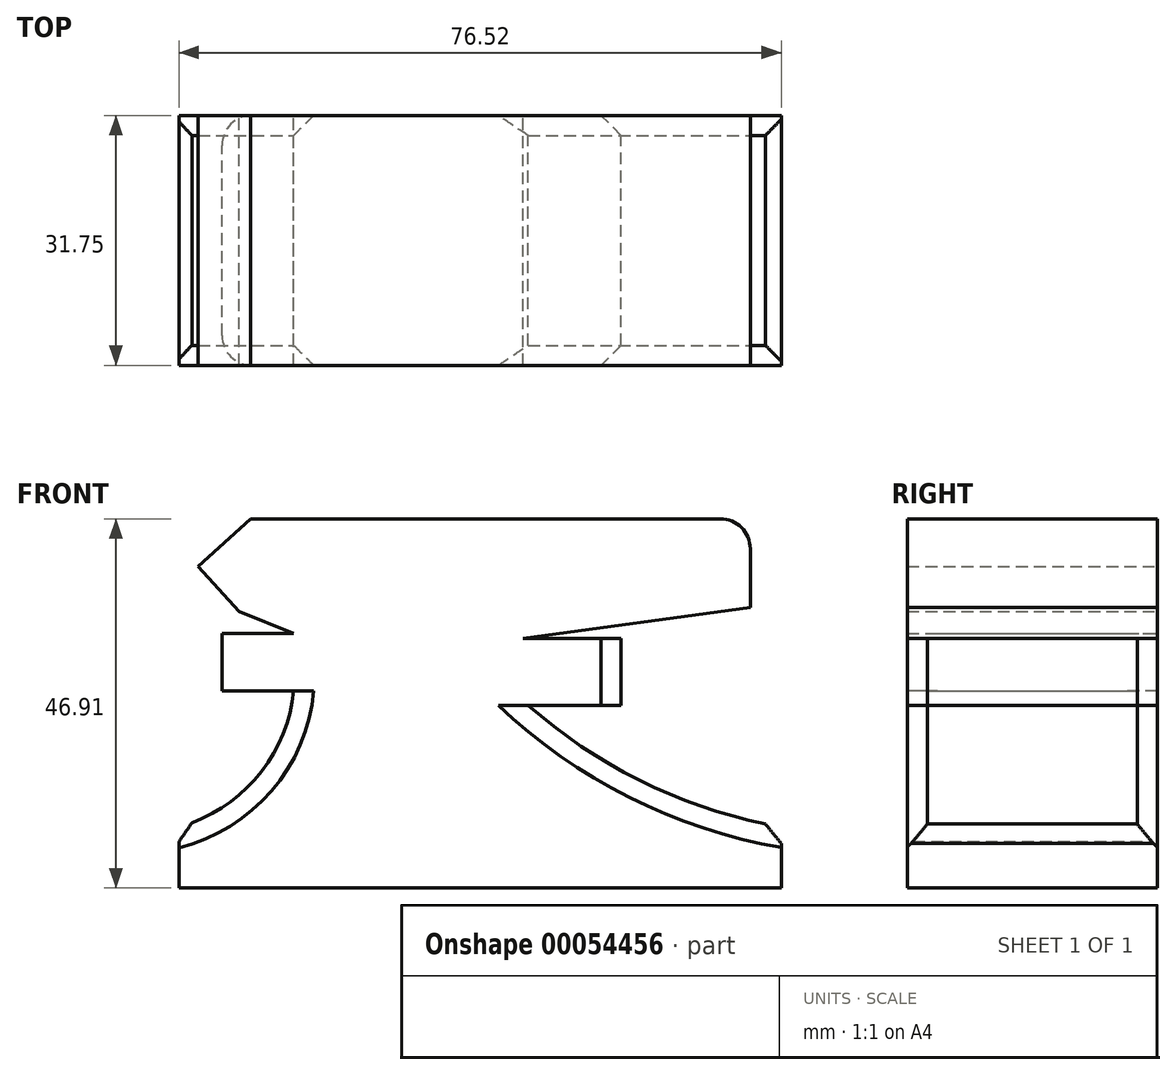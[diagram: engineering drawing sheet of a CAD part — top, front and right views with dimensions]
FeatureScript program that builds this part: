
annotation { "Feature Type Name" : "Feature", "Feature Type Description" : "" }
export const myFeature = defineFeature(function(context is Context, id is Id, definition is map)
    precondition{}
    {
        {
            var Q0;
            Q0=qCreatedBy(makeId("Front.planeOp"),FACE);
            var sketch = newSketch(context, id + "F0", { "sketchPlane" : qUnion([Q0])});
            skLineSegment(sketch, "E0", {"start": v(0, 0) * mm, "end": v(41.6, 0) * mm});
            skLineSegment(sketch, "E1", {"start": v(41.6, 0) * mm, "end": v(41.6, 7.74) * mm});
            skArc(sketch, "E2", {"start": v(9.41, 23.23) * mm, "mid": v(24.45, 13.28) * mm, "end": v(41.6, 7.74) * mm});
            skLineSegment(sketch, "E3", {"start": v(9.41, 23.23) * mm, "end": v(21.26, 23.23) * mm});
            skLineSegment(sketch, "E4", {"start": v(21.26, 23.23) * mm, "end": v(21.26, 31.73) * mm});
            skLineSegment(sketch, "E5", {"start": v(21.26, 31.73) * mm, "end": v(8.8, 31.73) * mm});
            skLineSegment(sketch, "E6", {"start": v(8.8, 31.73) * mm, "end": v(37.65, 35.68) * mm});
            skLineSegment(sketch, "E7", {"start": v(37.65, 35.68) * mm, "end": v(37.65, 46.91) * mm});
            skLineSegment(sketch, "E8", {"start": v(37.65, 46.91) * mm, "end": v(-25.8, 46.91) * mm});
            skLineSegment(sketch, "E9", {"start": v(-25.8, 46.91) * mm, "end": v(-32.49, 40.84) * mm});
            skLineSegment(sketch, "E10", {"start": v(-32.49, 40.84) * mm, "end": v(-27.31, 35.14) * mm});
            skLineSegment(sketch, "E11", {"start": v(-27.31, 35.14) * mm, "end": v(-20.34, 32.34) * mm});
            skLineSegment(sketch, "E12", {"start": v(-20.34, 32.34) * mm, "end": v(-29.45, 32.34) * mm});
            skLineSegment(sketch, "E13", {"start": v(-29.45, 32.34) * mm, "end": v(-29.45, 25.05) * mm});
            skLineSegment(sketch, "E14", {"start": v(-29.45, 25.05) * mm, "end": v(-20.34, 25.05) * mm});
            skArc(sketch, "E15", {"start": v(-34.92, 7.74) * mm, "mid": v(-24.96, 14.15) * mm, "end": v(-20.34, 25.05) * mm});
            skLineSegment(sketch, "E16", {"start": v(-34.92, 7.74) * mm, "end": v(-34.92, 0) * mm});
            skLineSegment(sketch, "E17", {"start": v(-34.92, 0) * mm, "end": v(0, 0) * mm});
            skSolve(sketch);
        }
        {
            var Q0;
            Q0=makeQuery(id+"F0.imprint","IMPRINT",FACE,{"disambiguationData":[TD([[makeQuery(id+"F0.imprint","IMPRINT",EDGE,{"derivedFrom":sQuery(id+"F0.wireOp",EDGE,"E0")}),1.0]])]});
            extrude(context, id + "F1", {"entities" : qUnion([Q0]), "depth" : 31.75 * mm});
        }
        {
            var Q0;
            Q0=makeQuery(id+"F1.opExtrude","CAP_EDGE",EDGE,{"disambiguationData":[OSD([sQuery(id+"F0.wireOp",EDGE,"E2")])],"isStart":false});
            var Q1;
            Q1=makeQuery(id+"F1.opExtrude","CAP_EDGE",EDGE,{"disambiguationData":[OSD([sQuery(id+"F0.wireOp",EDGE,"E2")])],"isStart":true});
            var Q2;
            Q2=makeQuery(id+"F1.opExtrude","CAP_EDGE",EDGE,{"disambiguationData":[OSD([sQuery(id+"F0.wireOp",EDGE,"E15")])],"isStart":false});
            var Q3;
            Q3=makeQuery(id+"F1.opExtrude","CAP_EDGE",EDGE,{"disambiguationData":[OSD([sQuery(id+"F0.wireOp",EDGE,"E15")])],"isStart":true});
            var Q4;
            Q4=makeQuery(id+"F1.opExtrude","SWEPT_EDGE",EDGE,{"disambiguationData":[OSD([sQuery(id+"F0.wireOp",EDGE,"E1"),sQuery(id+"F0.wireOp",EDGE,"E2")])]});
            var Q5;
            Q5=makeQuery(id+"F1.opExtrude","SWEPT_EDGE",EDGE,{"disambiguationData":[OSD([sQuery(id+"F0.wireOp",EDGE,"E15"),sQuery(id+"F0.wireOp",EDGE,"E16")])]});
            var Q6;
            Q6=makeQuery(id+"F1.opExtrude","CAP_EDGE",EDGE,{"disambiguationData":[OSD([sQuery(id+"F0.wireOp",EDGE,"E4")])],"isStart":true});
            var Q7;
            Q7=makeQuery(id+"F1.opExtrude","CAP_EDGE",EDGE,{"disambiguationData":[OSD([sQuery(id+"F0.wireOp",EDGE,"E4")])],"isStart":false});
            chamfer(context, id + "F2", {"entities" : qUnion([Q0, Q1, Q2, Q3, Q4, Q5, Q6, Q7]), "width" : 2.54 * mm, "tangentPropagation" : true});
        }
        {
            var Q0;
            Q0=makeQuery(id+"F1.opExtrude","CAP_EDGE",EDGE,{"disambiguationData":[OSD([sQuery(id+"F0.wireOp",EDGE,"E13")])],"isStart":false});
            var Q1;
            Q1=makeQuery(id+"F1.opExtrude","CAP_EDGE",EDGE,{"disambiguationData":[OSD([sQuery(id+"F0.wireOp",EDGE,"E13")])],"isStart":true});
            var Q2;
            Q2=makeQuery(id+"F1.opExtrude","SWEPT_EDGE",EDGE,{"disambiguationData":[OSD([sQuery(id+"F0.wireOp",EDGE,"E7"),sQuery(id+"F0.wireOp",EDGE,"E8")])]});
            fillet(context, id + "F3", {"entities" : qUnion([Q0, Q1, Q2]), "radius" : 3.8 * mm, "tangentPropagation" : true, "allowEdgeOverflow" : false});
        }
    });
